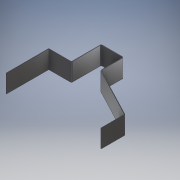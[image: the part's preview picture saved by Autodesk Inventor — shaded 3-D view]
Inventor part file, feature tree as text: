
AUTODESK INVENTOR PART (.ipt)
format: ipt  version: 2018 (Build 220112000, 112)  size: 130,560 bytes
history: native  units: mm
features: other x1, extrude x1, sketch x1
ambient origin geometry x8: Origin, YZ Plane, XZ Plane, XY Plane, X Axis, Y Axis, Z Axis, Center Point
bodies: Body1 (feature_tree)
feature tree (3):
  other  "Sólido1"
  extrude  "Extrusión1"  Depth=2.0mm
  sketch  "Boceto1"  dims[d1=75.0mm d2=0.0mm d3=2.0mm d4=2.0mm]
